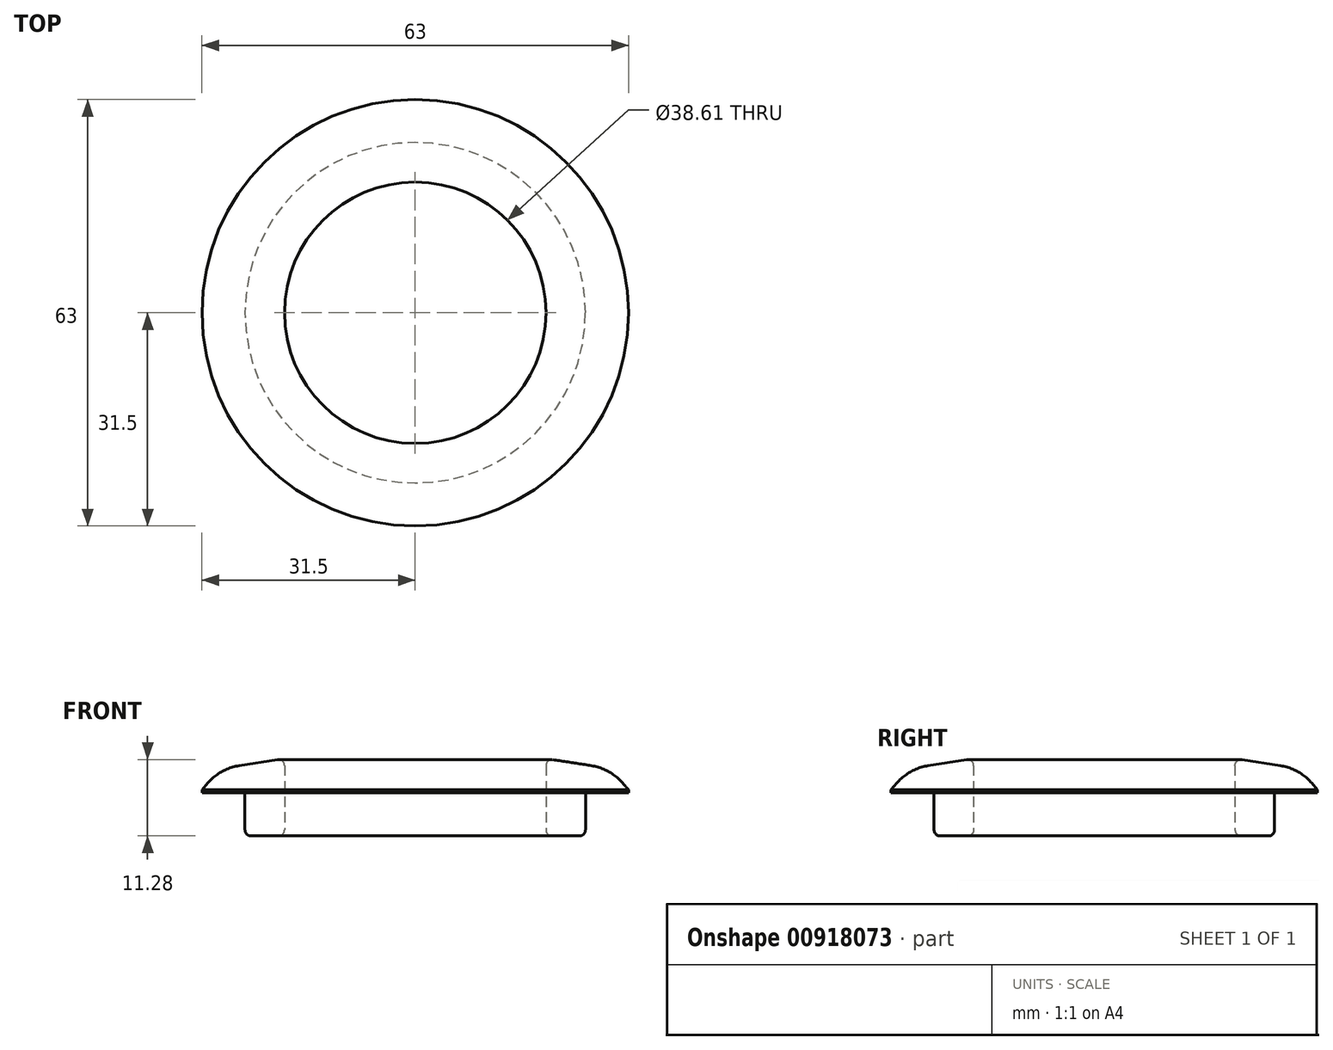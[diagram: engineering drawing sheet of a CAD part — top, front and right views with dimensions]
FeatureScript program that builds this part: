
annotation { "Feature Type Name" : "Feature", "Feature Type Description" : "" }
export const myFeature = defineFeature(function(context is Context, id is Id, definition is map)
    precondition{}
    {
        {
            var Q0;
            Q0=qCreatedBy(makeId("Front.planeOp"),FACE);
            var sketch = newSketch(context, id + "F0", { "sketchPlane" : qUnion([Q0])});
            skLineSegment(sketch, "E0", {"start": v(-25.15, 0) * mm, "end": v(-25.15, 6.35) * mm});
            skLineSegment(sketch, "E1", {"start": v(-25.15, 6.35) * mm, "end": v(-31.5, 6.35) * mm});
            skLineSegment(sketch, "E2", {"start": v(-31.5, 6.35) * mm, "end": v(-31.5, 9.52) * mm});
            skLineSegment(sketch, "E3", {"start": v(-31.5, 9.52) * mm, "end": v(-19.3, 11.43) * mm});
            skLineSegment(sketch, "E4", {"start": v(-19.3, 11.43) * mm, "end": v(-19.3, 0) * mm});
            skLineSegment(sketch, "E5", {"start": v(-19.3, 0) * mm, "end": v(-25.15, 0) * mm});
            skLineSegment(sketch, "E6", {"start": v(0, 0) * mm, "end": v(0, 96.64) * mm});
            skSolve(sketch);
        }
        {
            var Q0;
            Q0 = qSketchRegion(id + "F0", true);
            var Q1;
            Q1=sQuery(id+"F0.wireOp",EDGE,"E6");
            revolve(context, id + "F1", {"surfaceOperationType" : NewSurfaceOperationType.NEW, "entities" : qUnion([Q0]), "axis" : qUnion([Q1]), "revolveType" : RevolveType.FULL});
        }
        {
            var Q0;
            Q0=makeQuery(id+"F1.opRevolve","SWEPT_EDGE",EDGE,{"disambiguationData":[OSD([sQuery(id+"F0.wireOp",EDGE,"E2"),sQuery(id+"F0.wireOp",EDGE,"E3")])]});
            chamfer(context, id + "F2", {"entities" : qUnion([Q0]), "width" : 3.17 * mm, "tangentPropagation" : true});
        }
        {
            var Q0;
            {var subQ0=sQuery(id+"F0.wireOp",EDGE,"E3");Q0=makeQuery(id+"F2.opChamfer","BLEND_EDGE",EDGE,{"blendedFrom":[makeQuery(id+"F1.opRevolve","SWEPT_EDGE",EDGE,{"disambiguationData":[OSD([sQuery(id+"F0.wireOp",EDGE,"E2"),subQ0])]}),makeQuery(id+"F1.opRevolve","SWEPT_FACE",FACE,{"disambiguationData":[OSD([subQ0])]})],"blendedInto":[makeQuery(id+"F1.opRevolve","SWEPT_FACE",FACE,{"disambiguationData":[OSD([subQ0])]})]});}
            fillet(context, id + "F3", {"entities" : qUnion([Q0]), "tangentPropagation" : true, "radius" : 7.62 * mm, "defaultsChanged" : true, "vertexSettings" : [], "allowEdgeOverflow" : false});
        }
        {
            var Q0;
            Q0=makeQuery(id+"F1.opRevolve","SWEPT_EDGE",EDGE,{"disambiguationData":[OSD([sQuery(id+"F0.wireOp",EDGE,"E3"),sQuery(id+"F0.wireOp",EDGE,"E4")])]});
            var Q1;
            Q1=makeQuery(id+"F1.opRevolve","SWEPT_EDGE",EDGE,{"disambiguationData":[OSD([sQuery(id+"F0.wireOp",EDGE,"E4"),sQuery(id+"F0.wireOp",EDGE,"E5")])]});
            var Q2;
            Q2=makeQuery(id+"F1.opRevolve","SWEPT_EDGE",EDGE,{"disambiguationData":[OSD([sQuery(id+"F0.wireOp",EDGE,"E0"),sQuery(id+"F0.wireOp",EDGE,"E5")])]});
            fillet(context, id + "F4", {"entities" : qUnion([Q0, Q1, Q2]), "tangentPropagation" : true, "radius" : 0.89 * mm, "defaultsChanged" : true, "vertexSettings" : [], "allowEdgeOverflow" : false});
        }
    });
